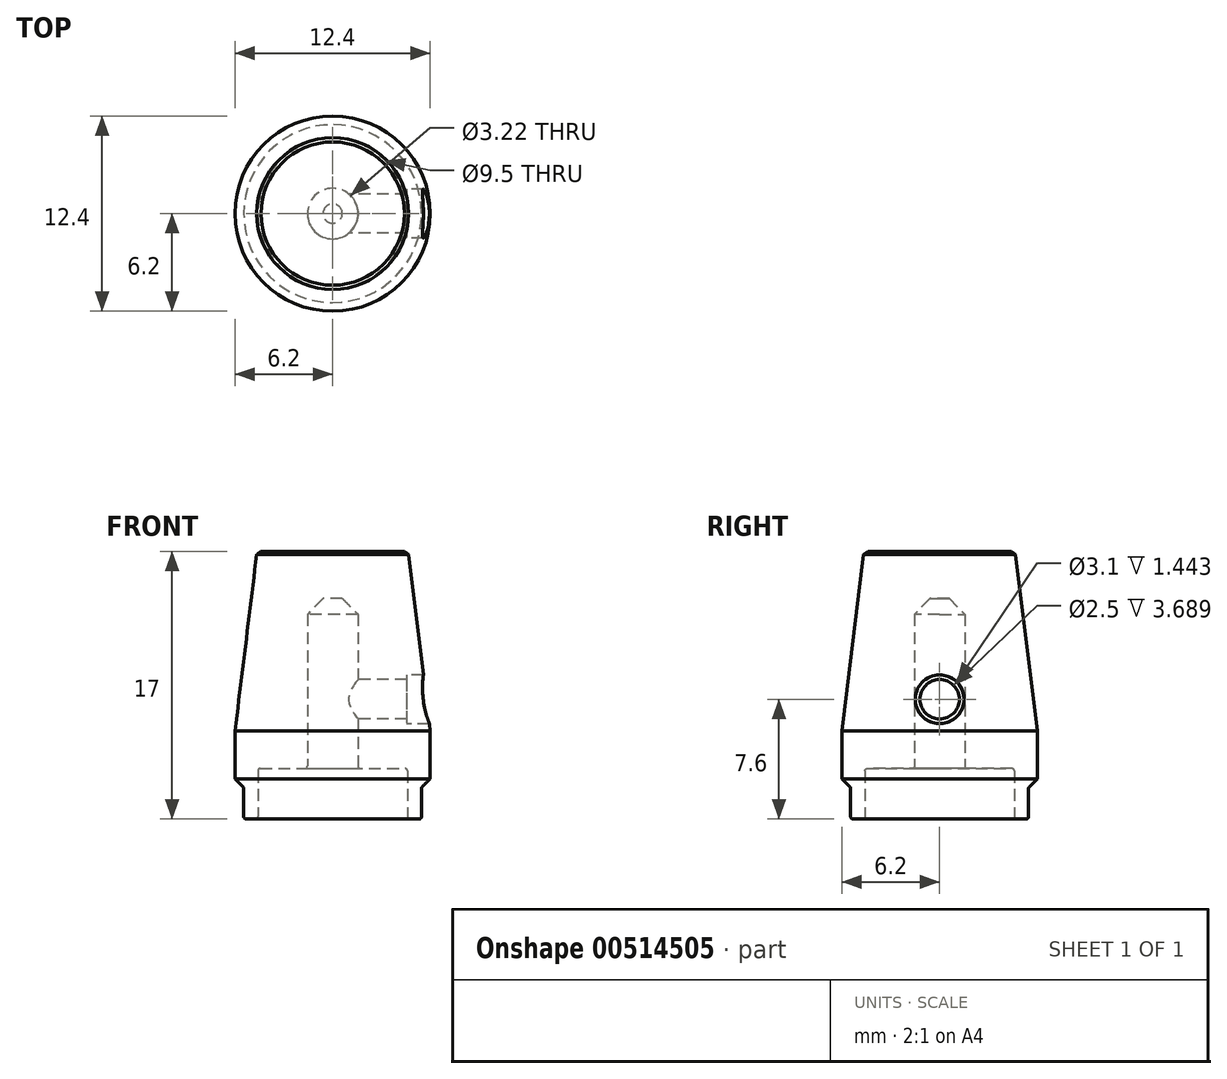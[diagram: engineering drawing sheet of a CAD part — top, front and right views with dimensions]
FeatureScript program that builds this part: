
annotation { "Feature Type Name" : "Feature", "Feature Type Description" : "" }
export const myFeature = defineFeature(function(context is Context, id is Id, definition is map)
    precondition{}
    {
        {
            var Q0;
            Q0=qCreatedBy(makeId("Front.planeOp"),FACE);
            var sketch = newSketch(context, id + "F0", { "sketchPlane" : qUnion([Q0])});
            skLineSegment(sketch, "E0.bottom", {"start": v(4.75, 0) * mm, "end": v(5.65, 0) * mm});
            skLineSegment(sketch, "E0.top", {"start": v(0, 17) * mm, "end": v(4.8, 17) * mm});
            skLineSegment(sketch, "E0.left", {"start": v(0, 3.2) * mm, "end": v(0, 17) * mm, "construction": true});
            skLineSegment(sketch, "E0.right", {"start": v(6.2, 2) * mm, "end": v(6.2, 5.6) * mm});
            skLineSegment(sketch, "E1", {"start": v(1.6, 3.2) * mm, "end": v(4.75, 3.2) * mm});
            skLineSegment(sketch, "E2", {"start": v(4.75, 3.2) * mm, "end": v(4.75, 0) * mm});
            skLineSegment(sketch, "E3", {"start": v(5.65, 0) * mm, "end": v(5.65, 2) * mm});
            skLineSegment(sketch, "E4", {"start": v(5.65, 2) * mm, "end": v(6.2, 2) * mm});
            skLineSegment(sketch, "E5", {"start": v(1.6, 3.2) * mm, "end": v(1.6, 14) * mm});
            skLineSegment(sketch, "E6", {"start": v(1.6, 14) * mm, "end": v(0, 14) * mm});
            skLineSegment(sketch, "E7", {"start": v(0, 17) * mm, "end": v(0, 14) * mm});
            skPoint(sketch, "E8", {"position": v(0, 7.6) * mm});
            skLineSegment(sketch, "E9", {"start": v(4.8, 17) * mm, "end": v(6.2, 5.6) * mm});
            skLineSegment(sketch, "E10", {"start": v(6.2, 5.6) * mm, "end": v(6.2, 20.36) * mm, "construction": true});
            skPoint(sketch, "E11", {"position": v(0, 0) * mm});
            skLineSegment(sketch, "E12", {"start": v(0, 7.6) * mm, "end": v(6.2, 7.6) * mm, "construction": true});
            skPoint(sketch, "E13", {"position": v(6.2, 7.6) * mm});
            skSolve(sketch);
        }
        {
            var Q0;
            Q0=qSketchRegion(id+"F0",true);
            var Q1;
            Q1=sQuery(id+"F0.wireOp",EDGE,"E0.left");
            revolve(context, id + "F1", {"entities" : qUnion([Q0]), "axis" : qUnion([Q1]), "revolveType" : RevolveType.FULL});
        }
        {
            var Q0;
            Q0=makeQuery(id+"F1.opRevolve","SWEPT_EDGE",EDGE,{"disambiguationData":[OSD([sQuery(id+"F0.wireOp",EDGE,"E0.right"),sQuery(id+"F0.wireOp",EDGE,"E4")])]});
            chamfer(context, id + "F2", {"entities" : qUnion([Q0]), "width" : .55 * mm});
        }
        {
            var Q0;
            Q0=makeQuery(id+"F1.opRevolve","SWEPT_EDGE",EDGE,{"disambiguationData":[OSD([sQuery(id+"F0.wireOp",EDGE,"E5"),sQuery(id+"F0.wireOp",EDGE,"E6")])]});
            chamfer(context, id + "F3", {"entities" : qUnion([Q0]), "width" : 1 * mm, "tangentPropagation" : true});
        }
        {
            var Q0;
            Q0=makeQuery(id+"F1.opRevolve","SWEPT_EDGE",EDGE,{"disambiguationData":[OSD([sQuery(id+"F0.wireOp",EDGE,"E0.top"),sQuery(id+"F0.wireOp",EDGE,"E9")])]});
            chamfer(context, id + "F4", {"entities" : qUnion([Q0]), "chamferType" : ChamferType.TWO_OFFSETS, "width1" : .25 * mm, "oppositeDirection" : false, "width2" : .2 * mm, "tangentPropagation" : true});
        }
        {
            var Q0;
            Q0=makeQuery(id+"F1.opRevolve","SWEPT_FACE",FACE,{"disambiguationData":[OSD([sQuery(id+"F0.wireOp",EDGE,"E0.bottom")])]});
            var Q1;
            Q1=makeQuery(id+"F1.opRevolve","SWEPT_EDGE",EDGE,{"disambiguationData":[OSD([sQuery(id+"F0.wireOp",EDGE,"E1"),sQuery(id+"F0.wireOp",EDGE,"E2")])]});
            var Q2;
            Q2=makeQuery(id+"F1.opRevolve","SWEPT_EDGE",EDGE,{"disambiguationData":[OSD([sQuery(id+"F0.wireOp",EDGE,"E1"),sQuery(id+"F0.wireOp",EDGE,"E5")])]});
            var Q3;
            Q3=makeQuery(id+"F2.opChamfer","BLEND_EDGE",EDGE,{"blendedFrom":[makeQuery(id+"F1.opRevolve","SWEPT_EDGE",EDGE,{"disambiguationData":[OSD([sQuery(id+"F0.wireOp",EDGE,"E0.right"),sQuery(id+"F0.wireOp",EDGE,"E4")])]}),makeQuery(id+"F1.opRevolve","SWEPT_FACE",FACE,{"disambiguationData":[OSD([sQuery(id+"F0.wireOp",EDGE,"E3")])]})],"blendedInto":[makeQuery(id+"F1.opRevolve","SWEPT_FACE",FACE,{"disambiguationData":[OSD([sQuery(id+"F0.wireOp",EDGE,"E3")])]})]});
            fillet(context, id + "F5", {"entities" : qUnion([Q0, Q1, Q2, Q3]), "radius" : 0.15 * mm, "tangentPropagation" : true, "allowEdgeOverflow" : false});
        }
        {
            var Q0;
            Q0=sQuery(id+"F0.wireOp",EDGE,"E0.right");
            cPlane(context, id + "F6", {"entities" : qUnion([Q0]), "cplaneType" : CPlaneType.LINE_ANGLE, "offset" : 25 * mm, "angle" : 0 * degree, "width" : 150 * mm, "height" : 150 * mm});
        }
        {
            var Q0;
            Q0=qCreatedBy(id+"F6.planeOp",FACE);
            var sketch = newSketch(context, id + "F7", { "sketchPlane" : qUnion([Q0])});
            skPoint(sketch, "E14.0", {"position": v(0, 7.6) * mm});
            skSolve(sketch);
        }
        {
            var Q0;
            Q0=sQuery(id+"F7.wireOp",VERTEX,"E14.0");
            var Q1;
            Q1=makeQuery(id+"F1.opRevolve","SWEPT_BODY",BODY,{"disambiguationData":[OSD([sQuery(id+"F0.wireOp",EDGE,"E0.bottom"),sQuery(id+"F0.wireOp",EDGE,"E0.top"),sQuery(id+"F0.wireOp",EDGE,"E0.right"),sQuery(id+"F0.wireOp",EDGE,"E1"),sQuery(id+"F0.wireOp",EDGE,"E2"),sQuery(id+"F0.wireOp",EDGE,"E3"),sQuery(id+"F0.wireOp",EDGE,"E4"),sQuery(id+"F0.wireOp",EDGE,"E5"),sQuery(id+"F0.wireOp",EDGE,"E6"),sQuery(id+"F0.wireOp",EDGE,"E7"),sQuery(id+"F0.wireOp",EDGE,"E9")])]});
            hole(context, id + "F8", {"style" : HoleStyle.C_BORE, "endStyle" : HoleEndStyle.BLIND, "holeDiameter" : 2.5 * mm, "cBoreDiameter" : 3.1 * mm, "cBoreDepth" : 1 * mm, "holeDepth" : 5 * mm, "isTappedThrough" : true, "tappedDepth" : 12 * mm, "tapClearance" : 3, "locations" : qUnion([Q0]), "scope" : qUnion([Q1]), "startStyle" : HoleStartStyle.PART});
        }
    });
